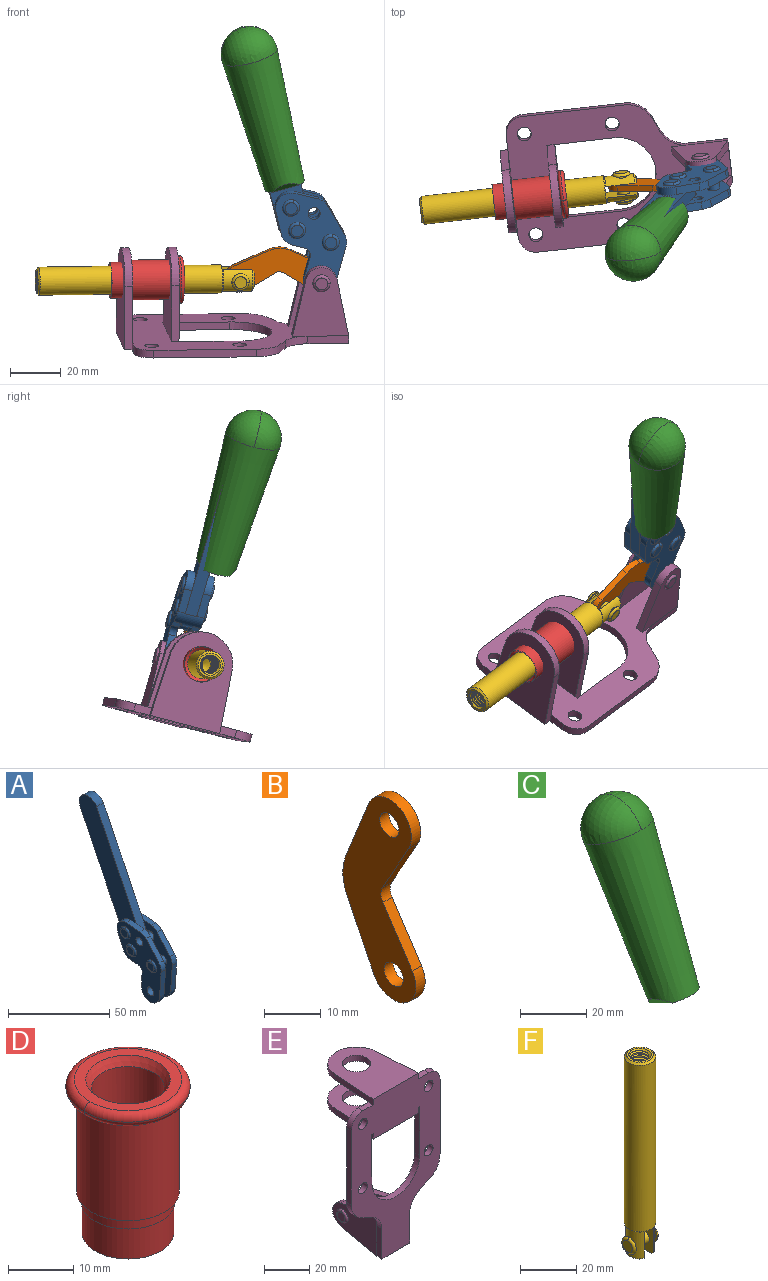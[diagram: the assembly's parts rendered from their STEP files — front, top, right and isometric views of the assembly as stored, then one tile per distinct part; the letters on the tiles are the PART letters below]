
ASSEMBLY  parts=6 mates=6
PART A: 59 faces, bbox 12.9x60.2x99.6 mm
  f0: torus R=2.39mm, axis (-1,0,0), area 14.9mm2, adj f20,f43,f51
  f1: torus R=2.39mm, axis (-1,0,0), area 14.9mm2, adj f19,f42,f51
  f2: torus R=2.39mm, axis (-1,0,0), area 14.9mm2, adj f18,f35,f51
  f3: torus R=2.39mm, axis (-1,0,0), area 14.9mm2, adj f14,f17,f23
  f4: torus R=2.39mm, axis (-1,0,0), area 14.9mm2, adj f13,f16,f23
  f5: torus R=2.39mm, axis (-1,0,0), area 14.9mm2, adj f12,f15,f23
  f6: cylinder r=2.39mm len=4.78mm, axis (1,0,0), area 46.5mm2, adj f48,f50,f51
  f7: cylinder r=2.39mm len=4.78mm, axis (1,0,0), area 46.5mm2, adj f50,f51
  f8: cylinder r=6.35mm len=12.68mm, axis (1,0,0), area 61.8mm2, adj f38,f39,f50,f51
  f9: cylinder r=2.39mm len=4.78mm, axis (-1,0,0), area 70.5mm2, adj f46,f50
  f10: cylinder r=2.39mm len=4.78mm, axis (-1,0,0), area 46.5mm2, adj f23,f45,f46
  f11: cylinder r=2.39mm len=4.78mm, axis (-1,0,0), area 46.5mm2, adj f23,f46
  f12: plane 4.78x4.78mm, normal (1,0,0), area 17.9mm2, adj f5,f15
  f13: plane 4.78x4.78mm, normal (1,0,0), area 17.9mm2, adj f4,f16
  f14: plane 4.78x4.78mm, normal (1,0,0), area 17.9mm2, adj f3,f17
  f15: torus R=2.39mm, axis (-1,0,0), area 14.9mm2, adj f5,f12,f23
  f16: torus R=2.39mm, axis (-1,0,0), area 14.9mm2, adj f4,f13,f23
  f17: torus R=2.39mm, axis (-1,0,0), area 14.9mm2, adj f3,f14,f23
  f18: plane 4.78x4.78mm, normal (-1,0,0), area 17.9mm2, adj f2,f35
  f19: plane 4.78x4.78mm, normal (-1,0,0), area 17.9mm2, adj f1,f42
  f20: plane 4.78x4.78mm, normal (-1,0,0), area 17.9mm2, adj f0,f43
  f21: plane 2.26x0.2mm, normal (1,0,0), area 0.2mm2, adj f31,f44
  f22: plane 2.26x0.2mm, normal (-1,0,0), area 0.2mm2, adj f41,f44
  f23: plane 39.37x30.77mm, normal (1,0,0), area 565.5mm2, adj f3,f4,f5,f10,f11,f15,f16,f17
  f24: cylinder r=6.1mm len=4.15mm, axis (-1,0,0), area 14.7mm2, adj f23,f25,f32,f46
  f25: plane 10.25x9.01mm, normal (0,-0.75,0.66), area 42.3mm2, adj f23,f24,f26,f46
  f26: cylinder r=6.35mm len=4.64mm, axis (-1,0,0), area 15.6mm2, adj f23,f25,f27,f46
  f27: plane 15.84x3.1mm, normal (0,-1,-0.07), area 49.2mm2, adj f23,f26,f28,f46
  f28: cylinder r=6.35mm len=12.68mm, axis (-1,0,0), area 61.8mm2, adj f23,f27,f29,f46
  f29: plane 8.11x3.1mm, normal (0,1,0.07), area 25.2mm2, adj f23,f28,f30,f46
  f30: cylinder r=3.05mm len=3.25mm, axis (-1,0,0), area 14.8mm2, adj f23,f29,f31,f46
  f31: plane 5.99x3.1mm, normal (0,0.07,-1), area 18.6mm2, adj f21,f23,f30,f44,f46
  f32: plane 9.5x3.1mm, normal (0,-0.07,1), area 29.5mm2, adj f23,f24,f33,f46,f47
  f33: cylinder r=6.1mm len=8.63mm, axis (-1,0,0), area 39.1mm2, adj f23,f32,f34,f47
  f34: plane 8.65x3.96mm, normal (0,0.91,-0.42), area 29.5mm2, adj f23,f33,f44,f47
  f35: torus R=2.39mm, axis (-1,0,0), area 14.9mm2, adj f2,f18,f51
  f36: plane 10.25x9.01mm, normal (0,-0.75,0.66), area 42.3mm2, adj f37,f49,f50,f51
  f37: cylinder r=6.35mm len=4.64mm, axis (1,0,0), area 15.6mm2, adj f36,f38,f50,f51
  f38: plane 15.84x3.1mm, normal (0,-1,-0.07), area 49.2mm2, adj f8,f37,f50,f51
  f39: plane 8.11x3.1mm, normal (0,1,0.07), area 25.2mm2, adj f8,f40,f50,f51
  f40: cylinder r=3.05mm len=3.25mm, axis (1,0,0), area 14.8mm2, adj f39,f41,f50,f51
  f41: plane 5.99x3.1mm, normal (0,0.07,-1), area 18.6mm2, adj f22,f40,f44,f50,f51
  f42: torus R=2.39mm, axis (-1,0,0), area 14.9mm2, adj f1,f19,f51
  f43: torus R=2.39mm, axis (-1,0,0), area 14.9mm2, adj f0,f20,f51
  f44: cylinder r=6.35mm len=12.12mm, axis (-1,0,0), area 128.9mm2, adj f21,f22,f23,f31,f34,f41,f46,f47
  f45: plane 2.65x1.35mm, normal (1,0,0), area 1mm2, adj f10,f55
  f46: plane 39.08x20.42mm, normal (-1,0,0), area 412.5mm2, adj f9,f10,f11,f24,f25,f26,f27,f28
  f47: plane 77.62x39.82mm, normal (1,0,0), area 850mm2, adj f32,f33,f34,f44,f53,f54,f55
  f48: plane 2.65x1.35mm, normal (-1,0,0), area 1mm2, adj f6,f55
  f49: cylinder r=6.1mm len=4.15mm, axis (1,0,0), area 14.7mm2, adj f36,f50,f51,f56
  f50: plane 39.08x20.42mm, normal (1,0,0), area 412.5mm2, adj f6,f7,f8,f9,f36,f37,f38,f39
  f51: plane 39.37x30.77mm, normal (-1,0,0), area 565.5mm2, adj f0,f1,f2,f6,f7,f8,f35,f36
  f52: plane 8.65x3.96mm, normal (0,0.91,-0.42), area 29.5mm2, adj f44,f51,f57,f58
  f53: plane 68.49x33.4mm, normal (0,0.9,-0.44), area 358.1mm2, adj f44,f47,f54,f58
  f54: cylinder r=6.35mm len=12.06mm, axis (1,0,0), area 93.7mm2, adj f47,f53,f55,f58
  f55: plane 68.49x33.4mm, normal (0,-0.9,0.44), area 358.1mm2, adj f44,f45,f46,f47,f48,f50,f54,f58
  f56: plane 9.5x3.1mm, normal (0,-0.07,1), area 29.5mm2, adj f49,f50,f51,f57,f58
  f57: cylinder r=6.1mm len=8.63mm, axis (1,0,0), area 39.1mm2, adj f51,f52,f56,f58
  f58: plane 77.62x39.82mm, normal (-1,0,0), area 850mm2, adj f44,f52,f53,f54,f55,f56,f57
PART B: 12 faces, bbox 2.3x18.2x42.8 mm
  f0: cylinder r=2.4mm len=4.8mm, axis (1,0,0), area 34.9mm2, adj f4,f11
  f1: cylinder r=10.41mm len=8.47mm, axis (1,0,0), area 20.2mm2, adj f4,f9,f10,f11
  f2: cylinder r=3.05mm len=3.16mm, axis (1,0,0), area 7.7mm2, adj f4,f6,f7,f11
  f3: cylinder r=2.4mm len=4.8mm, axis (1,0,0), area 34.9mm2, adj f4,f11
  f4: plane 42.81x18.23mm, normal (-1,0,0), area 414.1mm2, adj f0,f1,f2,f3,f5,f6,f7,f8
  f5: cylinder r=5.54mm len=10.67mm, axis (1,0,0), area 41.8mm2, adj f4,f6,f10,f11
  f6: plane 11.66x6.53mm, normal (0,-0.87,-0.49), area 30.9mm2, adj f2,f4,f5,f11
  f7: plane 11.17x7.33mm, normal (0,-0.84,0.55), area 30.9mm2, adj f2,f4,f8,f11
  f8: cylinder r=5.54mm len=10.51mm, axis (1,0,0), area 41.8mm2, adj f4,f7,f9,f11
  f9: plane 13.67x6.67mm, normal (0,0.9,-0.44), area 35.1mm2, adj f1,f4,f8,f11
  f10: plane 14.1x5.7mm, normal (0,0.93,0.37), area 35.1mm2, adj f1,f4,f5,f11
  f11: plane 42.81x18.23mm, normal (1,0,0), area 414.1mm2, adj f0,f1,f2,f3,f5,f6,f7,f8
PART C: 11 faces, bbox 22.3x42.6x64.5 mm
  f0: sphere r=11.13mm, area 411.4mm2, adj f1,f8
  f1: cone r=11.11mm half-angle=3.3deg, axis (0,0.44,0.9), area 3251.8mm2, adj f0,f7,f8,f9,f10
  f2: cylinder r=6.16mm len=11.7mm, axis (1,0,0), area 89.5mm2, adj f3,f4,f5,f6
  f3: plane 60.23x36.75mm, normal (-1,0,0), area 763.6mm2, adj f2,f4,f6,f10
  f4: plane 51.37x25.05mm, normal (0,0.9,-0.44), area 264.2mm2, adj f2,f3,f5,f10
  f5: plane 60.23x36.75mm, normal (1,0,0), area 763.6mm2, adj f2,f4,f6,f10
  f6: plane 51.37x25.05mm, normal (0,-0.9,0.44), area 264.2mm2, adj f2,f3,f5,f10
  f7: plane 9.95x5.95mm, normal (0.71,-0.31,-0.64), area 25.8mm2, adj f1,f10
  f8: sphere r=11.13mm, area 411.4mm2, adj f0,f1
  f9: plane 9.95x5.95mm, normal (-0.71,-0.31,-0.64), area 25.8mm2, adj f1,f10
  f10: plane 14.27x11.38mm, normal (0,-0.44,-0.9), area 106.7mm2, adj f1,f3,f4,f5,f6,f7,f9
PART D: 15 faces, bbox 20.6x20.6x28.7 mm
  f0: torus R=8.26mm, axis (0,0,1), area 56.8mm2, adj f1,f10,f12
  f1: torus R=8.26mm, axis (0,0,1), area 56.8mm2, adj f0,f6,f13
  f2: cylinder r=5.59mm len=25.91mm, axis (0,0,1), area 909.6mm2, adj f3,f4
  f3: cone r=6.86mm half-angle=45deg, axis (0,0,-1), area 70.2mm2, adj f2,f14
  f4: cone r=6.47mm half-angle=30deg, axis (0,0,1), area 66.7mm2, adj f2,f13
  f5: cylinder r=7.04mm len=14.07mm, axis (0,0,1), area 252.6mm2, adj f11,f14
  f6: torus R=8.26mm, axis (0,0,1), area 56.8mm2, adj f1,f12,f13
  f7: cylinder r=7.16mm len=14.33mm, axis (0,0,1), area 91.5mm2, adj f9,f11
  f8: cylinder r=7.86mm len=18.42mm, axis (0,0,1), area 909.6mm2, adj f9,f10
  f9: plane 15.72x15.72mm, normal (0,0,-1), area 33mm2, adj f7,f8
  f10: plane 16.51x16.51mm, normal (0,0,-1), area 19.9mm2, adj f0,f8,f12
  f11: plane 14.33x14.33mm, normal (0,0,-1), area 5.7mm2, adj f5,f7
  f12: torus R=8.26mm, axis (0,0,1), area 56.8mm2, adj f0,f6,f10
  f13: plane 16.51x16.51mm, normal (0,0,1), area 82.7mm2, adj f1,f4,f6
  f14: plane 14.07x14.07mm, normal (0,0,-1), area 7.8mm2, adj f3,f5
PART E: 55 faces, bbox 55.7x37.4x89.8 mm
  f0: torus R=2.41mm, axis (-1,0,0), area 15mm2, adj f11,f15,f25
  f1: torus R=2.41mm, axis (-1,0,0), area 15mm2, adj f10,f12,f22
  f2: cylinder r=2.78mm len=5.56mm, axis (0,-1,0), area 54.2mm2, adj f30,f54
  f3: cylinder r=14.99mm len=29.97mm, axis (0,-1,0), area 145.9mm2, adj f30,f49,f53,f54
  f4: cylinder r=2.78mm len=5.56mm, axis (0,-1,0), area 54.2mm2, adj f30,f54
  f5: cylinder r=2.78mm len=5.56mm, axis (0,-1,0), area 54.2mm2, adj f30,f54
  f6: cylinder r=2.78mm len=5.56mm, axis (0,-1,0), area 54.2mm2, adj f30,f54
  f7: cylinder r=6.35mm len=12.7mm, axis (0,0,1), area 123.6mm2, adj f27,f51
  f8: cylinder r=6.35mm len=12.7mm, axis (0,0,-1), area 124.7mm2, adj f21,f35
  f9: cylinder r=2.41mm len=11.18mm, axis (-1,0,0), area 169.4mm2, adj f16,f19
  f10: plane 4.83x4.83mm, normal (1,0,0), area 18.3mm2, adj f1,f12
  f11: plane 4.83x4.83mm, normal (-1,0,0), area 18.3mm2, adj f0,f15
  f12: torus R=2.41mm, axis (-1,0,0), area 15mm2, adj f1,f10,f22
  f13: cylinder r=6.35mm len=12.41mm, axis (1,0,0), area 53.4mm2, adj f18,f19,f22,f23
  f14: cylinder r=6.35mm len=12.41mm, axis (-1,0,0), area 53.4mm2, adj f16,f17,f24,f25
  f15: torus R=2.41mm, axis (-1,0,0), area 15mm2, adj f0,f11,f25
  f16: plane 27.86x22.35mm, normal (1,0,0), area 425.4mm2, adj f9,f14,f17,f24,f30
  f17: plane 22.86x4.97mm, normal (0,0.21,0.98), area 72.5mm2, adj f14,f16,f25,f30
  f18: plane 22.86x4.97mm, normal (0,0.21,0.98), area 72.5mm2, adj f13,f19,f22,f30
  f19: plane 27.86x22.35mm, normal (-1,0,0), area 425.4mm2, adj f9,f13,f18,f23,f30
  f20: cylinder r=12.7mm len=25.35mm, axis (0,0,-1), area 119.8mm2, adj f21,f34,f35,f36
  f21: plane 34.21x28.07mm, normal (0,0,-1), area 702.4mm2, adj f8,f20,f30,f34,f36
  f22: plane 27.96x22.45mm, normal (1,0,0), area 407.2mm2, adj f1,f12,f13,f18,f23,f30,f42,f43
  f23: plane 22.86x4.97mm, normal (0,0.21,-0.98), area 72.5mm2, adj f13,f19,f22,f44
  f24: plane 22.86x4.97mm, normal (0,0.21,-0.98), area 72.5mm2, adj f14,f16,f25,f44
  f25: plane 27.86x22.35mm, normal (-1,0,0), area 407.1mm2, adj f0,f14,f15,f17,f24,f30,f45,f46
  f26: plane 3.1x0.95mm, normal (0,0,-1), area 2.7mm2, adj f30,f49,f50,f54
  f27: plane 34.21x28.07mm, normal (0,0,1), area 702.4mm2, adj f7,f28,f30,f50,f52
  f28: cylinder r=12.7mm len=25.35mm, axis (0,0,1), area 118.8mm2, adj f27,f50,f51,f52
  f29: plane 3.1x0.95mm, normal (0,0,-1), area 2.7mm2, adj f30,f52,f53,f54
  f30: plane 86.54x55.63mm, normal (0,1,0), area 2362.9mm2, adj f2,f3,f4,f5,f6,f16,f17,f18
  f31: plane 40.56x3.1mm, normal (-1,0,0), area 125.7mm2, adj f30,f32,f48,f54
  f32: cylinder r=7.11mm len=7.11mm, axis (0,-1,0), area 34.6mm2, adj f30,f31,f33,f54
  f33: plane 6.67x3.1mm, normal (0,0,1), area 20.4mm2, adj f30,f32,f34,f54
  f34: plane 25.39x3.13mm, normal (-1,0.06,0), area 79.5mm2, adj f20,f21,f33,f35,f54
  f35: plane 37.31x28.45mm, normal (0,0,1), area 789.9mm2, adj f8,f20,f34,f36,f54
  f36: plane 25.39x3.13mm, normal (1,0.06,0), area 79.5mm2, adj f20,f21,f35,f37,f54
  f37: plane 6.67x3.1mm, normal (0,0,1), area 20.4mm2, adj f30,f36,f38,f54
  f38: cylinder r=7.11mm len=7.11mm, axis (0,-1,0), area 34.6mm2, adj f30,f37,f39,f54
  f39: plane 40.56x3.1mm, normal (1,0,0), area 125.7mm2, adj f30,f38,f40,f54
  f40: cylinder r=11.18mm len=10.16mm, axis (0,-1,0), area 39.5mm2, adj f30,f39,f41,f54
  f41: plane 6.09x3.1mm, normal (0.42,0,-0.91), area 20.8mm2, adj f30,f40,f42,f54
  f42: cylinder r=11.18mm len=9.41mm, axis (0,-1,0), area 37.2mm2, adj f22,f30,f41,f43,f54
  f43: plane 16.5x3.1mm, normal (1,0,0), area 51.1mm2, adj f22,f42,f44,f54
  f44: plane 17.37x3.1mm, normal (0,0,-1), area 53.8mm2, adj f23,f24,f30,f43,f45,f54
  f45: plane 16.5x3.1mm, normal (-1,0,0), area 51.1mm2, adj f25,f44,f46,f54
  f46: cylinder r=11.18mm len=9.41mm, axis (0,-1,0), area 37.2mm2, adj f25,f30,f45,f47,f54
  f47: plane 6.09x3.1mm, normal (-0.42,0,-0.91), area 20.8mm2, adj f30,f46,f48,f54
  f48: cylinder r=11.18mm len=10.16mm, axis (0,-1,0), area 39.5mm2, adj f30,f31,f47,f54
  f49: plane 26.54x3.1mm, normal (-1,0,0), area 82.3mm2, adj f3,f26,f30,f54
  f50: plane 25.39x3.1mm, normal (1,0.06,0), area 78.8mm2, adj f26,f27,f28,f51,f54
  f51: plane 37.31x28.45mm, normal (0,0,-1), area 789.9mm2, adj f7,f28,f50,f52,f54
  f52: plane 25.39x3.1mm, normal (-1,0.06,0), area 78.8mm2, adj f27,f28,f29,f51,f54
  f53: plane 26.54x3.1mm, normal (1,0,0), area 82.3mm2, adj f3,f29,f30,f54
  f54: plane 89.66x55.63mm, normal (0,-1,0), area 2678.5mm2, adj f2,f3,f4,f5,f6,f26,f29,f31
PART F: 48 faces, bbox 12.6x11.1x86.1 mm
  f0: torus R=2.41mm, axis (-1,0,0), area 15mm2, adj f30,f32,f34
  f1: torus R=2.41mm, axis (-1,0,0), area 15mm2, adj f29,f31,f33
  f2: cylinder r=5.54mm len=72.39mm, axis (0,0,1), area 2518.5mm2, adj f3,f4,f42,f43
  f3: cone r=5.54mm half-angle=45deg, axis (0,0,1), area 7.6mm2, adj f2,f5,f41
  f4: cone r=5.54mm half-angle=45deg, axis (0,0,-1), area 34.9mm2, adj f2,f39
  f5: cylinder r=5.08mm len=11.48mm, axis (0,0,1), area 108.3mm2, adj f3,f7,f8,f41
  f6: cylinder r=2.41mm len=4.83mm, axis (-1,0,0), area 71.2mm2, adj f40,f41
  f7: cylinder r=2.41mm len=4.83mm, axis (-1,0,0), area 7.6mm2, adj f5,f34
  f8: cone r=5.08mm half-angle=45deg, axis (0,0,1), area 10.6mm2, adj f5,f37,f41
  f9: cone r=3.98mm half-angle=45deg, axis (0,0,1), area 17.6mm2, adj f27,f39,f45,f46,f47
  f10: cylinder r=2.41mm len=4.83mm, axis (-1,0,0), area 7.6mm2, adj f33,f38
  f11: cylinder r=3.2mm len=6.4mm, axis (0,0,1), area 78.4mm2, adj f12,f28,f44,f45,f47
  f12: cylinder r=3.2mm len=6.4mm, axis (0,0,1), area 10.5mm2, adj f11,f13,f45,f47
  f13: cylinder r=3.2mm len=6.4mm, axis (0,0,1), area 10.5mm2, adj f12,f14,f45,f47
  f14: cylinder r=3.2mm len=6.4mm, axis (0,0,1), area 10.5mm2, adj f13,f15,f45,f47
  f15: cylinder r=3.2mm len=6.4mm, axis (0,0,1), area 10.5mm2, adj f14,f16,f45,f47
  f16: cylinder r=3.2mm len=6.4mm, axis (0,0,1), area 10.5mm2, adj f15,f17,f45,f47
  f17: cylinder r=3.2mm len=6.4mm, axis (0,0,1), area 10.5mm2, adj f16,f18,f45,f47
  f18: cylinder r=3.2mm len=6.4mm, axis (0,0,1), area 10.5mm2, adj f17,f19,f45,f47
  f19: cylinder r=3.2mm len=6.4mm, axis (0,0,1), area 10.5mm2, adj f18,f20,f45,f47
  f20: cylinder r=3.2mm len=6.4mm, axis (0,0,1), area 10.5mm2, adj f19,f21,f45,f47
  f21: cylinder r=3.2mm len=6.4mm, axis (0,0,1), area 10.5mm2, adj f20,f22,f45,f47
  f22: cylinder r=3.2mm len=6.4mm, axis (0,0,1), area 10.5mm2, adj f21,f23,f45,f47
  f23: cylinder r=3.2mm len=6.4mm, axis (0,0,1), area 10.5mm2, adj f22,f24,f45,f47
  f24: cylinder r=3.2mm len=6.4mm, axis (0,0,1), area 10.5mm2, adj f23,f25,f45,f47
  f25: cylinder r=3.2mm len=6.4mm, axis (0,0,1), area 10.5mm2, adj f24,f26,f45,f47
  f26: cylinder r=3.2mm len=6.4mm, axis (0,0,1), area 10.5mm2, adj f25,f27,f45,f47
  f27: cylinder r=3.2mm len=6.4mm, axis (0,0,1), area 7.4mm2, adj f9,f26,f45,f47
  f28: cone r=3.2mm half-angle=60deg, axis (0,0,1), area 37.2mm2, adj f11
  f29: plane 4.83x4.83mm, normal (-1,0,0), area 18.3mm2, adj f1,f31
  f30: plane 4.83x4.83mm, normal (1,0,0), area 18.3mm2, adj f0,f32
  f31: torus R=2.41mm, axis (-1,0,0), area 15mm2, adj f1,f29,f33
  f32: torus R=2.41mm, axis (-1,0,0), area 15mm2, adj f0,f30,f34
  f33: plane 6.83x6.83mm, normal (1,0,0), area 18.3mm2, adj f1,f10,f31
  f34: plane 6.83x6.83mm, normal (-1,0,0), area 18.3mm2, adj f0,f7,f32
  f35: cone r=5.08mm half-angle=45deg, axis (0,0,1), area 10.6mm2, adj f36,f38,f40
  f36: plane 7.25x1.97mm, normal (0,0,-1), area 10mm2, adj f35,f40
  f37: plane 7.25x1.97mm, normal (0,0,-1), area 10mm2, adj f8,f41
  f38: cylinder r=5.08mm len=11.48mm, axis (0,0,1), area 108.3mm2, adj f10,f35,f40,f42
  f39: plane 9.55x9.55mm, normal (0,0,1), area 22mm2, adj f4,f9
  f40: plane 12.76x10.09mm, normal (1,0,0), area 95.7mm2, adj f6,f35,f36,f38,f42,f43
  f41: plane 12.76x10.09mm, normal (-1,0,0), area 95.7mm2, adj f3,f5,f6,f8,f37,f43
  f42: cone r=5.54mm half-angle=45deg, axis (0,0,1), area 7.6mm2, adj f2,f38,f40
  f43: plane 11.07x4.7mm, normal (0,0,-1), area 50.4mm2, adj f2,f40,f41
  f44: plane 0.89x0.62mm, normal (-1,0,0), area 0.3mm2, adj f11,f45,f46,f47
  f45: bspline ~24.8x7.63mm, area 266.6mm2, adj f9,f11,f12,f13,f14,f15,f16,f17
  f46: bspline ~24.87x7.63mm, area 73.6mm2, adj f9,f44,f45,f47
  f47: bspline ~24.98x7.63mm, area 272.5mm2, adj f9,f11,f12,f13,f14,f15,f16,f17
PLACE A rot(axis=(0.2,-0.03,0.98),99deg) t=(277.95,230.3,-29.5)mm
PLACE B rot(axis=(0.67,-0.46,-0.59),126.5deg) t=(231.99,237.68,-79.67)mm
PLACE C rot(axis=(0.2,-0.03,0.98),99deg) t=(278.47,225.82,-30.67)mm
PLACE D rot(axis=(-0.71,0.05,-0.71),165.1deg) t=(142.6,244.29,-51.54)mm
PLACE E rot(axis=(0.66,-0.45,-0.6),125.2deg) t=(215.55,234.83,-80.7)mm
PLACE F rot(axis=(0.66,-0.45,-0.6),125.2deg) t=(231.27,236.62,-80.51)mm fixed
MATE fastened D.f2 <-> E.f7  axis (0.99,0.11,0.01) through (191.45,225.86,-57.18)mm
MATE revolute B.f3 <-> E.f0  axis (-0.11,0.96,0.25) through (247.85,232.26,-56.49)mm
MATE fastened C.f2 <-> A.f54  axis (0.11,-0.96,-0.25) through (219.74,204.5,33.74)mm
MATE slider F.f2 <-> E.f7  axis (-0.99,-0.11,-0.01) through (173.28,223.8,-57.4)mm
MATE revolute B.f5 <-> F.f6  axis (0.11,-0.96,-0.25) through (216.31,228.68,-56.88)mm
MATE revolute A.f7 <-> E.f0  axis (0.11,-0.96,-0.25) through (247.85,232.26,-56.49)mm
